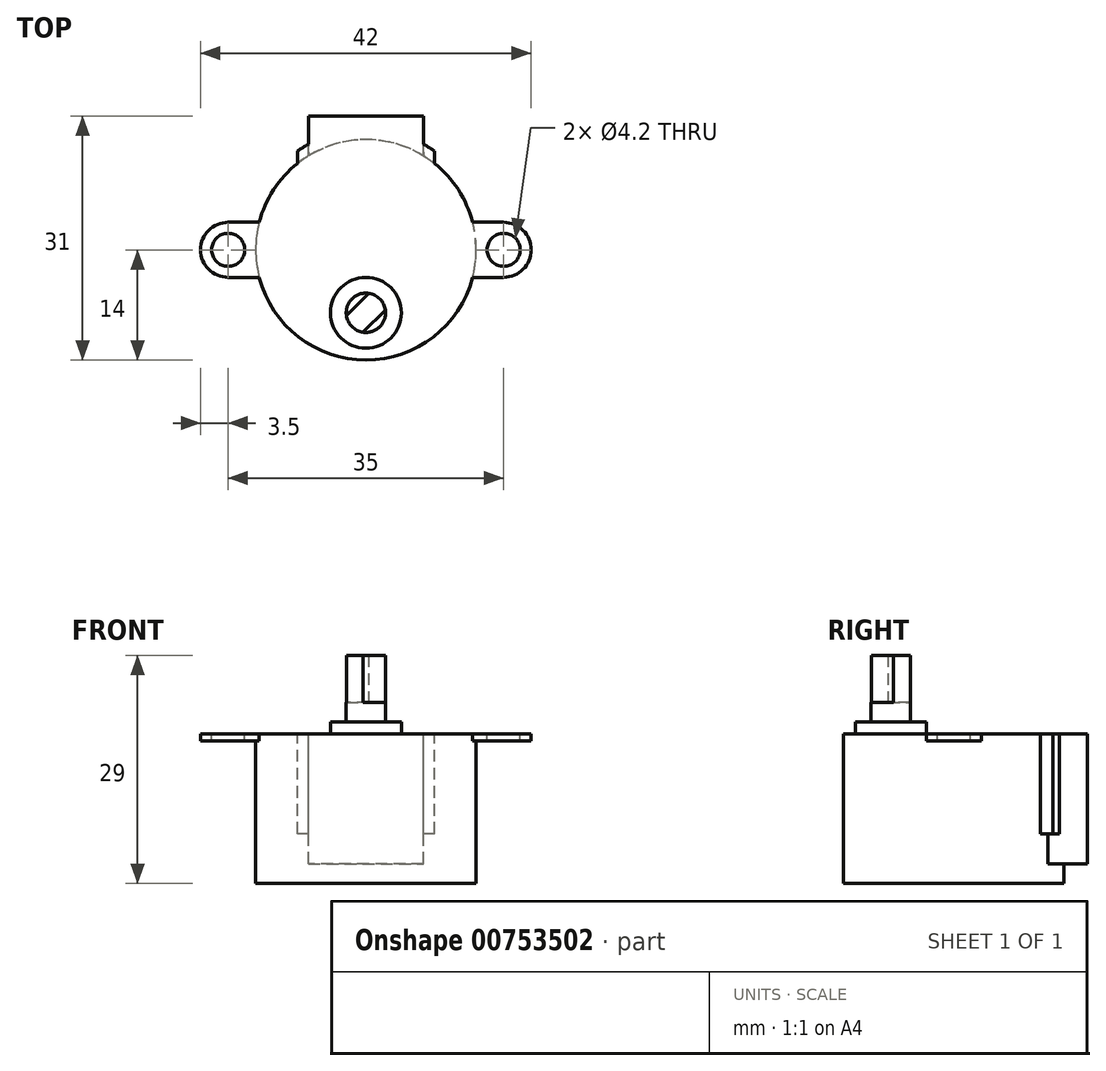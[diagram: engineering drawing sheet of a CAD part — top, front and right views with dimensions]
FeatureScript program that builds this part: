
annotation { "Feature Type Name" : "Feature", "Feature Type Description" : "" }
export const myFeature = defineFeature(function(context is Context, id is Id, definition is map)
    precondition{}
    {
        {
            var Q0;
            Q0=qCreatedBy(makeId("Top.planeOp"),FACE);
            var sketch = newSketch(context, id + "F0", { "sketchPlane" : qUnion([Q0])});
            skCircle(sketch, "E0", {"center": v(0, 0) * mm, "radius": 14 * mm});
            skSolve(sketch);
        }
        {
            var Q0;
            Q0=qCreatedBy(makeId("Top.planeOp"),FACE);
            var sketch = newSketch(context, id + "F1", { "sketchPlane" : qUnion([Q0])});
            skArc(sketch, "E1", {"start": v(8.69, 10.98) * mm, "mid": v(0, 14) * mm, "end": v(-8.69, 10.98) * mm});
            skLineSegment(sketch, "E2", {"start": v(-8.69, 10.98) * mm, "end": v(-8.69, 12.56) * mm});
            skLineSegment(sketch, "E3", {"start": v(8.69, 10.98) * mm, "end": v(8.69, 12.56) * mm});
            skArc(sketch, "E4", {"start": v(8.69, 12.56) * mm, "mid": v(0, 15.27) * mm, "end": v(-8.69, 12.56) * mm});
            skLineSegment(sketch, "E5", {"start": v(-8.69, 10.98) * mm, "end": v(8.69, 10.98) * mm, "construction": true});
            skSolve(sketch);
        }
        {
            var Q0;
            Q0=qCreatedBy(makeId("Top.planeOp"),FACE);
            var sketch = newSketch(context, id + "F2", { "sketchPlane" : qUnion([Q0])});
            skLineSegment(sketch, "E6.bottom", {"start": v(-7.3, 17) * mm, "end": v(7.3, 17) * mm});
            skLineSegment(sketch, "E6.top", {"start": v(-7.3, 11.95) * mm, "end": v(7.3, 11.95) * mm});
            skLineSegment(sketch, "E6.left", {"start": v(-7.3, 17) * mm, "end": v(-7.3, 11.95) * mm});
            skLineSegment(sketch, "E6.right", {"start": v(7.3, 17) * mm, "end": v(7.3, 11.95) * mm});
            skSolve(sketch);
        }
        {
            var Q0;
            Q0=qCreatedBy(makeId("Top.planeOp"),FACE);
            var sketch = newSketch(context, id + "F3", { "sketchPlane" : qUnion([Q0])});
            skLineSegment(sketch, "E7.bottom", {"start": v(-17.5, 3.5) * mm, "end": v(17.5, 3.5) * mm});
            skLineSegment(sketch, "E7.top", {"start": v(-17.5, -3.5) * mm, "end": v(17.5, -3.5) * mm});
            skLineSegment(sketch, "E7.left", {"start": v(-17.5, 3.5) * mm, "end": v(-17.5, -3.5) * mm, "construction": true});
            skLineSegment(sketch, "E7.right", {"start": v(17.5, 3.5) * mm, "end": v(17.5, -3.5) * mm, "construction": true});
            skArc(sketch, "E8", {"start": v(-17.5, 3.5) * mm, "mid": v(-21, 0) * mm, "end": v(-17.5, -3.5) * mm});
            skArc(sketch, "E9", {"start": v(17.5, -3.5) * mm, "mid": v(21, 0) * mm, "end": v(17.5, 3.5) * mm});
            skCircle(sketch, "E10", {"center": v(-17.5, 0) * mm, "radius": 2.1 * mm});
            skCircle(sketch, "E11", {"center": v(17.5, 0) * mm, "radius": 2.1 * mm});
            skSolve(sketch);
        }
        {
            var Q0;
            Q0=qCreatedBy(makeId("Top.planeOp"),FACE);
            var sketch = newSketch(context, id + "F4", { "sketchPlane" : qUnion([Q0])});
            skCircle(sketch, "E12", {"center": v(0, -8) * mm, "radius": 4.5 * mm});
            skLineSegment(sketch, "E13", {"start": v(-2.47, -8.35) * mm, "end": v(0.35, -5.53) * mm});
            skLineSegment(sketch, "E14", {"start": v(0.35, -5.53) * mm, "end": v(2.47, -7.65) * mm});
            skLineSegment(sketch, "E15", {"start": v(2.47, -7.65) * mm, "end": v(-0.35, -10.47) * mm});
            skLineSegment(sketch, "E16", {"start": v(-0.35, -10.47) * mm, "end": v(-2.47, -8.35) * mm});
            skArc(sketch, "E17", {"start": v(0.35, -5.53) * mm, "mid": v(-1.77, -6.23) * mm, "end": v(-2.47, -8.35) * mm});
            skArc(sketch, "E18", {"start": v(-0.35, -10.47) * mm, "mid": v(1.77, -9.77) * mm, "end": v(2.47, -7.65) * mm});
            skArc(sketch, "E19", {"start": v(2.47, -7.65) * mm, "mid": v(1.77, -6.23) * mm, "end": v(0.35, -5.53) * mm});
            skArc(sketch, "E20", {"start": v(-2.47, -8.35) * mm, "mid": v(-1.77, -9.77) * mm, "end": v(-0.35, -10.47) * mm});
            skSolve(sketch);
        }
        {
            var Q0;
            Q0=makeQuery(id+"F0.imprint","IMPRINT",FACE,{"disambiguationData":[TD([[makeQuery(id+"F0.imprint","IMPRINT",EDGE,{"derivedFrom":sQuery(id+"F0.wireOp",EDGE,"E0")}),1.0]])]});
            extrude(context, id + "F5", {"entities" : qUnion([Q0]), "oppositeDirection" : true, "depth" : 19 * mm, "offsetDistance" : 25.4 * mm});
        }
        {
            var Q0;
            Q0=makeQuery(id+"F2.imprint","IMPRINT",FACE,{"disambiguationData":[TD([[makeQuery(id+"F2.imprint","IMPRINT",EDGE,{"derivedFrom":sQuery(id+"F2.wireOp",EDGE,"E6.bottom")}),-1.0]])]});
            var Q1;
            Q1=makeQuery(id+"F5.opExtrude","CAP_FACE",FACE,{"disambiguationData":[OSD([sQuery(id+"F0.wireOp",EDGE,"E0")])],"isStart":false});
            extrude(context, id + "F6", {"entities" : qUnion([Q0]), "operationType" : NewBodyOperationType.ADD, "oppositeDirection" : true, "depth" : 16.5 * mm, "endBoundEntityFace" : qUnion([Q1]), "offsetDistance" : 25.4 * mm});
        }
        {
            var Q0;
            Q0=makeQuery(id+"F1.imprint","IMPRINT",FACE,{"disambiguationData":[TD([[makeQuery(id+"F1.imprint","IMPRINT",EDGE,{"derivedFrom":sQuery(id+"F1.wireOp",EDGE,"E1")}),-1.0]])]});
            extrude(context, id + "F7", {"entities" : qUnion([Q0]), "operationType" : NewBodyOperationType.ADD, "oppositeDirection" : true, "depth" : 12.7 * mm, "offsetDistance" : 25.4 * mm});
        }
        {
            var Q0;
            Q0=makeQuery(id+"F3.imprint","IMPRINT",FACE,{"disambiguationData":[TD([[makeQuery(id+"F3.imprint","IMPRINT",EDGE,{"derivedFrom":sQuery(id+"F3.wireOp",EDGE,"E7.bottom")}),-1.0]])]});
            extrude(context, id + "F8", {"entities" : qUnion([Q0]), "operationType" : NewBodyOperationType.ADD, "oppositeDirection" : true, "depth" : 0.86 * mm, "offsetDistance" : 25.4 * mm});
        }
        {
            var Q0;
            Q0=makeQuery(id+"F4.imprint","IMPRINT",FACE,{"disambiguationData":[TD([[makeQuery(id+"F4.imprint","IMPRINT",EDGE,{"derivedFrom":sQuery(id+"F4.wireOp",EDGE,"E13")}),-1.0]])]});
            var Q1;
            Q1=makeQuery(id+"F4.imprint","IMPRINT",FACE,{"disambiguationData":[TD([[makeQuery(id+"F4.imprint","IMPRINT",EDGE,{"derivedFrom":sQuery(id+"F4.wireOp",EDGE,"E16")}),1.0]])]});
            var Q2;
            Q2=makeQuery(id+"F4.imprint","IMPRINT",FACE,{"disambiguationData":[TD([[makeQuery(id+"F4.imprint","IMPRINT",EDGE,{"derivedFrom":sQuery(id+"F4.wireOp",EDGE,"E14")}),1.0]])]});
            extrude(context, id + "F9", {"entities" : qUnion([Q0, Q1, Q2]), "operationType" : NewBodyOperationType.ADD, "depth" : 10 * mm, "offsetDistance" : 25.4 * mm});
        }
        {
            var Q0;
            Q0=makeQuery(id+"F4.imprint","IMPRINT",FACE,{"disambiguationData":[TD([[makeQuery(id+"F4.imprint","IMPRINT",EDGE,{"derivedFrom":sQuery(id+"F4.wireOp",EDGE,"E15")}),1.0]])]});
            var Q1;
            Q1=makeQuery(id+"F4.imprint","IMPRINT",FACE,{"disambiguationData":[TD([[makeQuery(id+"F4.imprint","IMPRINT",EDGE,{"derivedFrom":sQuery(id+"F4.wireOp",EDGE,"E13")}),1.0]])]});
            extrude(context, id + "F10", {"entities" : qUnion([Q0, Q1]), "operationType" : NewBodyOperationType.ADD, "depth" : (10 - 6) * mm, "offsetDistance" : 25.4 * mm});
        }
        {
            var Q0;
            Q0=makeQuery(id+"F4.imprint","IMPRINT",FACE,{"disambiguationData":[TD([[makeQuery(id+"F4.imprint","IMPRINT",EDGE,{"derivedFrom":sQuery(id+"F4.wireOp",EDGE,"E12")}),1.0]])]});
            var Q1;
            Q1=makeQuery(id+"F4.imprint","IMPRINT",FACE,{"disambiguationData":[TD([[makeQuery(id+"F4.imprint","IMPRINT",EDGE,{"derivedFrom":sQuery(id+"F4.wireOp",EDGE,"E15")}),1.0]])]});
            extrude(context, id + "F11", {"entities" : qUnion([Q0, Q1]), "operationType" : NewBodyOperationType.ADD, "depth" : 1.5 * mm, "offsetDistance" : 25.4 * mm});
        }
    });
